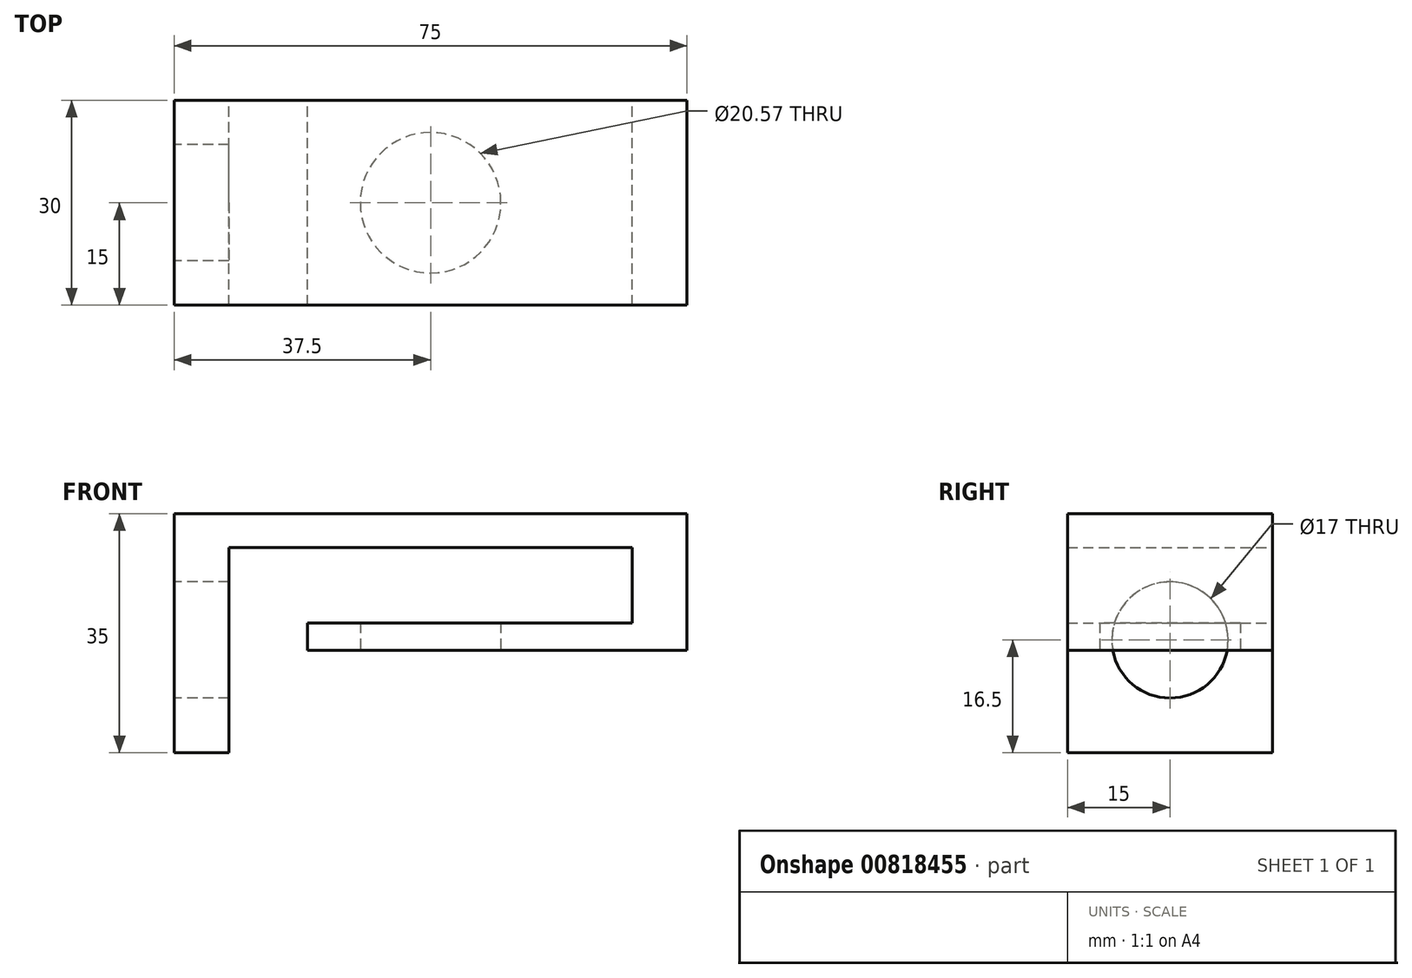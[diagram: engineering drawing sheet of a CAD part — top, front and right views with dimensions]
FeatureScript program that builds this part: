
annotation { "Feature Type Name" : "Feature", "Feature Type Description" : "" }
export const myFeature = defineFeature(function(context is Context, id is Id, definition is map)
    precondition{}
    {
        {
            var Q0;
            Q0=qCreatedBy(makeId("Front.planeOp"),FACE);
            var sketch = newSketch(context, id + "F0", { "sketchPlane" : qUnion([Q0])});
            skLineSegment(sketch, "E0.bottom", {"start": v(-37.5, 2.5) * mm, "end": v(37.5, 2.5) * mm});
            skLineSegment(sketch, "E0.top", {"start": v(-37.5, -2.5) * mm, "end": v(37.5, -2.5) * mm});
            skLineSegment(sketch, "E0.left", {"start": v(-37.5, 2.5) * mm, "end": v(-37.5, -2.5) * mm});
            skLineSegment(sketch, "E0.right", {"start": v(37.5, 2.5) * mm, "end": v(37.5, -2.5) * mm});
            skPoint(sketch, "E0.middle", {"position": v(0, 0) * mm});
            skLineSegment(sketch, "E1.bottom", {"start": v(-37.5, -2.5) * mm, "end": v(-29.5, -2.5) * mm});
            skLineSegment(sketch, "E1.top", {"start": v(-37.5, -32.5) * mm, "end": v(-29.5, -32.5) * mm});
            skLineSegment(sketch, "E1.left", {"start": v(-37.5, -2.5) * mm, "end": v(-37.5, -32.5) * mm});
            skLineSegment(sketch, "E1.right", {"start": v(-29.5, -2.5) * mm, "end": v(-29.5, -32.5) * mm});
            skLineSegment(sketch, "E2.bottom", {"start": v(37.5, -2.5) * mm, "end": v(29.5, -2.5) * mm});
            skLineSegment(sketch, "E2.top", {"start": v(37.5, -17.5) * mm, "end": v(29.5, -17.5) * mm});
            skLineSegment(sketch, "E2.left", {"start": v(37.5, -2.5) * mm, "end": v(37.5, -17.5) * mm});
            skLineSegment(sketch, "E2.right", {"start": v(29.5, -2.5) * mm, "end": v(29.5, -17.5) * mm});
            skLineSegment(sketch, "E3.bottom", {"start": v(29.5, -17.5) * mm, "end": v(-18, -17.5) * mm});
            skLineSegment(sketch, "E3.top", {"start": v(29.5, -13.5) * mm, "end": v(-18, -13.5) * mm});
            skLineSegment(sketch, "E3.left", {"start": v(29.5, -17.5) * mm, "end": v(29.5, -13.5) * mm});
            skLineSegment(sketch, "E3.right", {"start": v(-18, -17.5) * mm, "end": v(-18, -13.5) * mm});
            skSolve(sketch);
        }
        {
            var Q0;
            {var subQ5=sQuery(id+"F0.wireOp",EDGE,"E2.top");Q0=makeQuery(id+"F0.imprint","IMPRINT",FACE,{"disambiguationData":[TD([[makeQuery(id+"F0.imprint","IMPRINT",EDGE,{"derivedFrom":subQ5}),-1.0]])]});}
            var Q1;
            {var subQ0=sQuery(id+"F0.wireOp",EDGE,"E3.bottom");Q1=makeQuery(id+"F0.imprint","IMPRINT",FACE,{"disambiguationData":[TD([[makeQuery(id+"F0.imprint","IMPRINT",EDGE,{"derivedFrom":subQ0}),-1.0]])]});}
            var Q2;
            Q2=makeQuery(id+"F0.imprint","IMPRINT",FACE,{"disambiguationData":[TD([[makeQuery(id+"F0.imprint","IMPRINT",EDGE,{"derivedFrom":sQuery(id+"F0.wireOp",EDGE,"E0.bottom")}),-1.0]])]});
            var Q3;
            Q3=makeQuery(id+"F0.imprint","IMPRINT",FACE,{"disambiguationData":[TD([[makeQuery(id+"F0.imprint","IMPRINT",EDGE,{"derivedFrom":sQuery(id+"F0.wireOp",EDGE,"E1.top")}),1.0]])]});
            extrude(context, id + "F1", {"entities" : qUnion([Q0, Q1, Q2, Q3]), "depth" : 15 * mm, "offsetDistance" : 25 * mm});
        }
        {
            var Q0;
            Q0=makeQuery(id+"F1.opExtrude","SWEPT_BODY",BODY,{"disambiguationData":[OSD([sQuery(id+"F0.wireOp",EDGE,"E0.bottom"),sQuery(id+"F0.wireOp",EDGE,"E0.top"),sQuery(id+"F0.wireOp",EDGE,"E0.left"),sQuery(id+"F0.wireOp",EDGE,"E0.right"),sQuery(id+"F0.wireOp",EDGE,"E1.top"),sQuery(id+"F0.wireOp",EDGE,"E1.left"),sQuery(id+"F0.wireOp",EDGE,"E1.right"),sQuery(id+"F0.wireOp",EDGE,"E2.top"),sQuery(id+"F0.wireOp",EDGE,"E2.left"),sQuery(id+"F0.wireOp",EDGE,"E2.right"),sQuery(id+"F0.wireOp",EDGE,"E3.bottom"),sQuery(id+"F0.wireOp",EDGE,"E3.top"),sQuery(id+"F0.wireOp",EDGE,"E3.right")])]});
            var Q1;
            Q1=qCreatedBy(makeId("Front.planeOp"),FACE);
            mirror(context, id + "F2", {"operationType" : NewBodyOperationType.ADD, "entities" : qUnion([Q0]), "mirrorPlane" : qUnion([Q1])});
        }
        {
            var Q0;
            {var subQ0=makeQuery(id+"F1.opExtrude","SWEPT_FACE",FACE,{"disambiguationData":[OSD([sQuery(id+"F0.wireOp",EDGE,"E2.top"),sQuery(id+"F0.wireOp",EDGE,"E3.bottom")])]});Q0=makeQuery(id+"F2.boolean.opBoolean","MERGE",FACE,{"derivedFrom":[subQ0,makeQuery(id+"F2.opPattern","COPY",FACE,{"derivedFrom":subQ0,"instanceName":"1"})]});}
            var sketch = newSketch(context, id + "F3", { "sketchPlane" : qUnion([Q0])});
            skCircle(sketch, "E4", {"center": v(0, 0) * mm, "radius": 10.29 * mm});
            skSolve(sketch);
        }
        {
            var Q0;
            Q0=makeQuery(id+"F3.imprint","IMPRINT",FACE,{"disambiguationData":[TD([[makeQuery(id+"F3.imprint","IMPRINT",EDGE,{"derivedFrom":sQuery(id+"F3.wireOp",EDGE,"E4")}),1.0]])]});
            extrude(context, id + "F4", {"entities" : qUnion([Q0]), "operationType" : NewBodyOperationType.REMOVE, "oppositeDirection" : true, "depth" : 10 * mm, "offsetDistance" : 25 * mm});
        }
        {
            var Q0;
            {var subQ0=makeQuery(id+"F1.opExtrude","SWEPT_FACE",FACE,{"disambiguationData":[OSD([sQuery(id+"F0.wireOp",EDGE,"E0.left"),sQuery(id+"F0.wireOp",EDGE,"E1.left")])]});Q0=makeQuery(id+"F2.boolean.opBoolean","MERGE",FACE,{"derivedFrom":[subQ0,makeQuery(id+"F2.opPattern","COPY",FACE,{"derivedFrom":subQ0,"instanceName":"1"})]});}
            var sketch = newSketch(context, id + "F5", { "sketchPlane" : qUnion([Q0])});
            skLineSegment(sketch, "E5.bottom", {"start": v(-2.05, 2.5) * mm, "end": v(0.42, 2.5) * mm});
            skLineSegment(sketch, "E5.top", {"start": v(-2.05, -7.5) * mm, "end": v(0.42, -7.5) * mm});
            skLineSegment(sketch, "E5.left", {"start": v(-2.05, 2.5) * mm, "end": v(-2.05, -7.5) * mm});
            skLineSegment(sketch, "E5.right", {"start": v(0.42, 2.5) * mm, "end": v(0.42, -7.5) * mm});
            skCircle(sketch, "E6", {"center": v(0, -16) * mm, "radius": 8.5 * mm});
            skSolve(sketch);
        }
        {
            var Q0;
            Q0=makeQuery(id+"F5.imprint","IMPRINT",FACE,{"disambiguationData":[TD([[makeQuery(id+"F5.imprint","IMPRINT",EDGE,{"derivedFrom":sQuery(id+"F5.wireOp",EDGE,"E6")}),1.0]])]});
            extrude(context, id + "F6", {"entities" : qUnion([Q0]), "operationType" : NewBodyOperationType.REMOVE, "oppositeDirection" : true, "depth" : 10 * mm, "offsetDistance" : 25 * mm});
        }
    });
